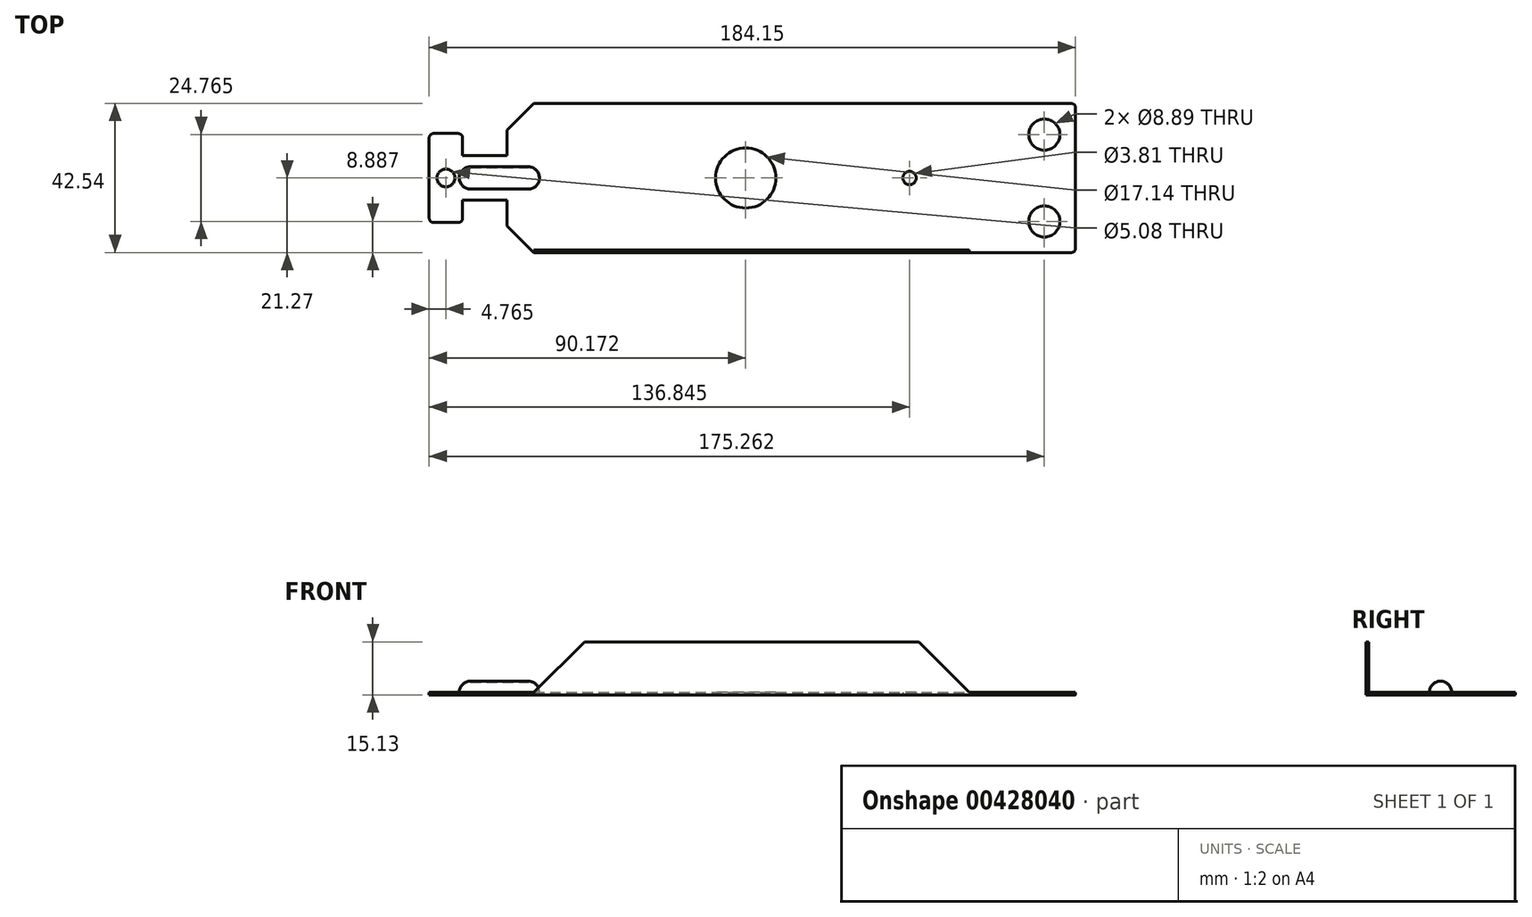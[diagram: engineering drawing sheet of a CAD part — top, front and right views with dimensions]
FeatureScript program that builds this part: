
annotation { "Feature Type Name" : "Feature", "Feature Type Description" : "" }
export const myFeature = defineFeature(function(context is Context, id is Id, definition is map)
    precondition{}
    {
        {
            var Q0;
            Q0=qCreatedBy(makeId("Top.planeOp"),FACE);
            var sketch = newSketch(context, id + "F0", { "sketchPlane" : qUnion([Q0])});
            skLineSegment(sketch, "E0.bottom", {"start": v(-80.96, 21.27) * mm, "end": v(79.7, 21.27) * mm});
            skLineSegment(sketch, "E0.top", {"start": v(-80.96, -21.27) * mm, "end": v(79.7, -21.27) * mm});
            skLineSegment(sketch, "E0.left", {"start": v(-80.96, 21.27) * mm, "end": v(-80.96, -21.27) * mm});
            skLineSegment(sketch, "E0.right", {"start": v(80.96, 20) * mm, "end": v(80.96, -20) * mm});
            skPoint(sketch, "E0.middle", {"position": v(0, 0) * mm});
            skLineSegment(sketch, "E1", {"start": v(-73.34, 21.27) * mm, "end": v(-80.96, 13.65) * mm});
            skLineSegment(sketch, "E2", {"start": v(-80.96, -13.65) * mm, "end": v(-73.34, -21.27) * mm});
            skCircle(sketch, "E3", {"center": v(-13.02, 0) * mm, "radius": 8.57 * mm});
            skCircle(sketch, "E4", {"center": v(33.66, 0) * mm, "radius": 1.9 * mm});
            skCircle(sketch, "E5", {"center": v(72.07, 12.38) * mm, "radius": 4.45 * mm});
            skCircle(sketch, "E6", {"center": v(72.07, -12.38) * mm, "radius": 4.45 * mm});
            skLineSegment(sketch, "E7.bottom", {"start": v(-98.43, 6.35) * mm, "end": v(-63.5, 6.35) * mm});
            skLineSegment(sketch, "E7.top", {"start": v(-98.43, -6.35) * mm, "end": v(-63.5, -6.35) * mm});
            skLineSegment(sketch, "E7.left", {"start": v(-98.43, 6.35) * mm, "end": v(-98.43, -6.35) * mm});
            skLineSegment(sketch, "E7.right", {"start": v(-63.5, 6.35) * mm, "end": v(-63.5, -6.35) * mm});
            skPoint(sketch, "E7.middle", {"position": v(-80.96, 0) * mm});
            skLineSegment(sketch, "E8.bottom", {"start": v(-101.92, 12.7) * mm, "end": v(-94.93, 12.7) * mm});
            skLineSegment(sketch, "E8.top", {"start": v(-101.92, -12.7) * mm, "end": v(-94.93, -12.7) * mm});
            skLineSegment(sketch, "E8.left", {"start": v(-103.19, 11.43) * mm, "end": v(-103.19, -11.43) * mm});
            skLineSegment(sketch, "E8.right", {"start": v(-93.66, 11.43) * mm, "end": v(-93.66, -11.43) * mm});
            skPoint(sketch, "E8.middle", {"position": v(-98.43, 0) * mm});
            skPoint(sketch, "E9.visualSharp", {"position": v(-103.19, 12.7) * mm});
            skArc(sketch, "E9.filletArc", {"start": v(-101.92, 12.7) * mm, "mid": v(-102.82, 12.33) * mm, "end": v(-103.19, 11.43) * mm});
            skPoint(sketch, "E10.visualSharp", {"position": v(-103.19, -12.7) * mm});
            skArc(sketch, "E10.filletArc", {"start": v(-103.19, -11.43) * mm, "mid": v(-102.82, -12.33) * mm, "end": v(-101.92, -12.7) * mm});
            skPoint(sketch, "E11.visualSharp", {"position": v(-93.66, -12.7) * mm});
            skArc(sketch, "E11.filletArc", {"start": v(-94.93, -12.7) * mm, "mid": v(-94.03, -12.33) * mm, "end": v(-93.66, -11.43) * mm});
            skPoint(sketch, "E12.visualSharp", {"position": v(-93.66, 12.7) * mm});
            skArc(sketch, "E12.filletArc", {"start": v(-93.66, 11.43) * mm, "mid": v(-94.03, 12.33) * mm, "end": v(-94.93, 12.7) * mm});
            skPoint(sketch, "E13.visualSharp", {"position": v(80.96, 21.27) * mm});
            skArc(sketch, "E13.filletArc", {"start": v(80.96, 20) * mm, "mid": v(80.6, 20.9) * mm, "end": v(79.7, 21.27) * mm});
            skPoint(sketch, "E14.visualSharp", {"position": v(80.96, -21.27) * mm});
            skArc(sketch, "E14.filletArc", {"start": v(79.7, -21.27) * mm, "mid": v(80.6, -20.9) * mm, "end": v(80.96, -20) * mm});
            skCircle(sketch, "E15", {"center": v(-98.43, 0) * mm, "radius": 2.54 * mm});
            skSolve(sketch);
        }
        {
            var Q0;
            Q0=makeQuery(id+"F0.imprint","IMPRINT",FACE,{"disambiguationData":[TD([[makeQuery(id+"F0.imprint","IMPRINT",EDGE,{"derivedFrom":sQuery(id+"F0.wireOp",EDGE,"E0.right")}),-1.0]])]});
            var Q1;
            {var subQ5=sQuery(id+"F0.wireOp",EDGE,"E7.right");Q1=makeQuery(id+"F0.imprint","IMPRINT",FACE,{"disambiguationData":[TD([[makeQuery(id+"F0.imprint","IMPRINT",EDGE,{"derivedFrom":subQ5}),-1.0]])]});}
            var Q2;
            {var subQ0=sQuery(id+"F0.wireOp",EDGE,"E7.bottom");var subQ1=sQuery(id+"F0.wireOp",EDGE,"E0.left");var subQ2=makeQuery(id+"F0.imprint","INTERSECT",VERTEX,{"derivedFrom":[subQ1,subQ0]});Q2=makeQuery(id+"F0.imprint","IMPRINT",FACE,{"disambiguationData":[TD([[makeQuery(id+"F0.imprint","IMPRINT",EDGE,{"disambiguationData":[TD([[subQ2,-1.0]])],"derivedFrom":subQ1}),-1.0]])]});}
            var Q3;
            {var subQ0=sQuery(id+"F0.wireOp",EDGE,"E7.left");var subQ1=sQuery(id+"F0.wireOp",EDGE,"E7.bottom");var subQ2=makeQuery(id+"F0.imprint","INTERSECT",VERTEX,{"derivedFrom":[subQ1,subQ0]});Q3=makeQuery(id+"F0.imprint","IMPRINT",FACE,{"disambiguationData":[TD([[makeQuery(id+"F0.imprint","IMPRINT",EDGE,{"disambiguationData":[TD([[subQ2,-1.0]])],"derivedFrom":subQ1}),-1.0]])]});}
            var Q4;
            Q4=makeQuery(id+"F0.imprint","IMPRINT",FACE,{"disambiguationData":[TD([[makeQuery(id+"F0.imprint","IMPRINT",EDGE,{"derivedFrom":sQuery(id+"F0.wireOp",EDGE,"E8.bottom")}),-1.0]])]});
            extrude(context, id + "F1", {"entities" : qUnion([Q0, Q1, Q2, Q3, Q4]), "depth" : 0.76 * mm});
        }
        {
            var Q0;
            Q0=makeQuery(id+"F1.opExtrude","SWEPT_FACE",FACE,{"disambiguationData":[OSD([sQuery(id+"F0.wireOp",EDGE,"E0.top")])]});
            var sketch = newSketch(context, id + "F2", { "sketchPlane" : qUnion([Q0])});
            skLineSegment(sketch, "E16", {"start": v(-73.34, 0.76) * mm, "end": v(-58.97, 15.13) * mm});
            skLineSegment(sketch, "E17", {"start": v(-58.97, 15.13) * mm, "end": v(36.28, 15.13) * mm});
            skLineSegment(sketch, "E18", {"start": v(36.28, 15.13) * mm, "end": v(50.64, 0.76) * mm});
            skSolve(sketch);
        }
        {
            var Q0;
            {var subQ0=sQuery(id+"F2.wireOp",EDGE,"E16");Q0=makeQuery(id+"F2.imprint","IMPRINT",FACE,{"disambiguationData":[TD([[makeQuery(id+"F2.imprint","IMPRINT",EDGE,{"derivedFrom":subQ0}),-1.0]])]});}
            extrude(context, id + "F3", {"entities" : qUnion([Q0]), "operationType" : NewBodyOperationType.ADD, "oppositeDirection" : true, "depth" : 0.76 * mm});
        }
        {
            var Q0;
            Q0=makeQuery(id+"F1.opExtrude","CAP_FACE",FACE,{"disambiguationData":[OSD([sQuery(id+"F0.wireOp",EDGE,"E0.bottom"),sQuery(id+"F0.wireOp",EDGE,"E0.top"),sQuery(id+"F0.wireOp",EDGE,"E0.left"),sQuery(id+"F0.wireOp",EDGE,"E0.right"),sQuery(id+"F0.wireOp",EDGE,"E1"),sQuery(id+"F0.wireOp",EDGE,"E2"),sQuery(id+"F0.wireOp",EDGE,"E3"),sQuery(id+"F0.wireOp",EDGE,"E4"),sQuery(id+"F0.wireOp",EDGE,"E5"),sQuery(id+"F0.wireOp",EDGE,"E6"),sQuery(id+"F0.wireOp",EDGE,"E7.bottom"),sQuery(id+"F0.wireOp",EDGE,"E7.top"),sQuery(id+"F0.wireOp",EDGE,"E8.bottom"),sQuery(id+"F0.wireOp",EDGE,"E8.top"),sQuery(id+"F0.wireOp",EDGE,"E8.left"),sQuery(id+"F0.wireOp",EDGE,"E8.right"),sQuery(id+"F0.wireOp",EDGE,"E9.filletArc"),sQuery(id+"F0.wireOp",EDGE,"E10.filletArc"),sQuery(id+"F0.wireOp",EDGE,"E11.filletArc"),sQuery(id+"F0.wireOp",EDGE,"E12.filletArc"),sQuery(id+"F0.wireOp",EDGE,"E13.filletArc"),sQuery(id+"F0.wireOp",EDGE,"E14.filletArc"),sQuery(id+"F0.wireOp",EDGE,"E15")])],"isStart":false});
            var sketch = newSketch(context, id + "F4", { "sketchPlane" : qUnion([Q0])});
            skLineSegment(sketch, "E19.bottom", {"start": v(-91.44, 3.18) * mm, "end": v(-74.93, 3.18) * mm});
            skLineSegment(sketch, "E19.top", {"start": v(-91.44, -3.17) * mm, "end": v(-74.93, -3.17) * mm});
            skLineSegment(sketch, "E19.left", {"start": v(-91.44, 3.18) * mm, "end": v(-91.44, -3.17) * mm});
            skLineSegment(sketch, "E19.right", {"start": v(-74.93, 3.18) * mm, "end": v(-74.93, -3.17) * mm});
            skArc(sketch, "E20", {"start": v(-91.44, 3.18) * mm, "mid": v(-94.62, 0) * mm, "end": v(-91.44, -3.17) * mm});
            skArc(sketch, "E21", {"start": v(-74.93, -3.17) * mm, "mid": v(-71.76, 0) * mm, "end": v(-74.93, 3.18) * mm});
            skArc(sketch, "E22.0.startCap", {"start": v(-91.44, 2.92) * mm, "mid": v(-91.7, 3.18) * mm, "end": v(-91.44, 3.43) * mm});
            skArc(sketch, "E22.0.endCap", {"start": v(-74.93, 3.43) * mm, "mid": v(-74.68, 3.18) * mm, "end": v(-74.93, 2.92) * mm});
            skLineSegment(sketch, "E22.0.left", {"start": v(-91.44, 3.43) * mm, "end": v(-74.93, 3.43) * mm});
            skLineSegment(sketch, "E22.0.right", {"start": v(-91.44, 2.92) * mm, "end": v(-74.93, 2.92) * mm});
            skArc(sketch, "E22.1.startCap", {"start": v(-91.44, 3.43) * mm, "mid": v(-91.19, 3.18) * mm, "end": v(-91.44, 2.92) * mm});
            skArc(sketch, "E22.1.endCap", {"start": v(-91.44, -2.92) * mm, "mid": v(-91.19, -3.17) * mm, "end": v(-91.44, -3.43) * mm});
            skArc(sketch, "E22.1.left", {"start": v(-91.44, 2.92) * mm, "mid": v(-94.36, 0) * mm, "end": v(-91.44, -2.92) * mm});
            skArc(sketch, "E22.1.right", {"start": v(-91.44, 3.43) * mm, "mid": v(-94.87, 0) * mm, "end": v(-91.44, -3.43) * mm});
            skArc(sketch, "E22.2.startCap", {"start": v(-91.44, -3.43) * mm, "mid": v(-91.7, -3.17) * mm, "end": v(-91.44, -2.92) * mm});
            skArc(sketch, "E22.2.endCap", {"start": v(-74.93, -2.92) * mm, "mid": v(-74.68, -3.17) * mm, "end": v(-74.93, -3.43) * mm});
            skLineSegment(sketch, "E22.2.left", {"start": v(-91.44, -2.92) * mm, "end": v(-74.93, -2.92) * mm});
            skLineSegment(sketch, "E22.2.right", {"start": v(-91.44, -3.43) * mm, "end": v(-74.93, -3.43) * mm});
            skArc(sketch, "E22.3.startCap", {"start": v(-74.93, -3.43) * mm, "mid": v(-75.18, -3.17) * mm, "end": v(-74.93, -2.92) * mm});
            skArc(sketch, "E22.3.endCap", {"start": v(-74.93, 2.92) * mm, "mid": v(-75.18, 3.18) * mm, "end": v(-74.93, 3.43) * mm});
            skArc(sketch, "E22.3.left", {"start": v(-74.93, -2.92) * mm, "mid": v(-72, 0) * mm, "end": v(-74.93, 2.92) * mm});
            skArc(sketch, "E22.3.right", {"start": v(-74.93, -3.43) * mm, "mid": v(-71.5, 0) * mm, "end": v(-74.93, 3.43) * mm});
            skLineSegment(sketch, "E23", {"start": v(-91.44, 0) * mm, "end": v(-74.93, 0) * mm});
            skLineSegment(sketch, "E24", {"start": v(-91.44, 0) * mm, "end": v(-94.87, 0) * mm});
            skLineSegment(sketch, "E25", {"start": v(-74.93, 0) * mm, "end": v(-71.5, 0) * mm});
            skSolve(sketch);
        }
        {
            var Q0;
            {var subQ0=sQuery(id+"F4.wireOp",EDGE,"E22.1.left");Q0=makeQuery(id+"F4.imprint","IMPRINT",FACE,{"disambiguationData":[TD([[makeQuery(id+"F4.imprint","IMPRINT",EDGE,{"derivedFrom":subQ0}),1.0]])]});}
            var Q1;
            {var subQ1=sQuery(id+"F4.wireOp",EDGE,"E22.0.right");Q1=makeQuery(id+"F4.imprint","IMPRINT",FACE,{"disambiguationData":[TD([[makeQuery(id+"F4.imprint","IMPRINT",EDGE,{"derivedFrom":subQ1}),-1.0]])]});}
            var Q2;
            {var subQ0=sQuery(id+"F4.wireOp",EDGE,"E22.3.left");Q2=makeQuery(id+"F4.imprint","IMPRINT",FACE,{"disambiguationData":[TD([[makeQuery(id+"F4.imprint","IMPRINT",EDGE,{"derivedFrom":subQ0}),1.0]])]});}
            var Q3;
            {var subQ0=sQuery(id+"F4.wireOp",EDGE,"E22.2.left");Q3=makeQuery(id+"F4.imprint","IMPRINT",FACE,{"disambiguationData":[TD([[makeQuery(id+"F4.imprint","IMPRINT",EDGE,{"derivedFrom":subQ0}),1.0]])]});}
            extrude(context, id + "F5", {"entities" : qUnion([Q0, Q1, Q2, Q3]), "operationType" : NewBodyOperationType.REMOVE, "oppositeDirection" : true, "depth" : 25.4 * mm});
        }
        {
            var Q0;
            {var subQ0=sQuery(id+"F4.wireOp",EDGE,"E22.2.endCap");var subQ1=sQuery(id+"F4.wireOp",EDGE,"E21");var subQ2=makeQuery(id+"F4.imprint","INTERSECT",VERTEX,{"derivedFrom":[subQ1,subQ0]});Q0=makeQuery(id+"F4.imprint","IMPRINT",FACE,{"disambiguationData":[TD([[makeQuery(id+"F4.imprint","IMPRINT",EDGE,{"disambiguationData":[TD([[subQ2,-1.0]])],"derivedFrom":subQ1}),1.0]])]});}
            var Q1;
            {var subQ0=sQuery(id+"F4.wireOp",EDGE,"E21");var subQ3=sQuery(id+"F4.wireOp",EDGE,"E22.2.endCap");var subQ5=makeQuery(id+"F4.imprint","INTERSECT",VERTEX,{"derivedFrom":[subQ0,subQ3]});Q1=makeQuery(id+"F4.imprint","IMPRINT",FACE,{"disambiguationData":[TD([[makeQuery(id+"F4.imprint","IMPRINT",EDGE,{"disambiguationData":[TD([[subQ5,1.0]])],"derivedFrom":subQ0}),1.0]])]});}
            var Q2;
            {var subQ1=sQuery(id+"F4.wireOp",EDGE,"E19.top");var subQ3=sQuery(id+"F4.wireOp",EDGE,"E22.3.startCap");var subQ4=makeQuery(id+"F4.imprint","INTERSECT",VERTEX,{"derivedFrom":[subQ1,subQ3]});Q2=makeQuery(id+"F4.imprint","IMPRINT",FACE,{"disambiguationData":[TD([[makeQuery(id+"F4.imprint","IMPRINT",EDGE,{"disambiguationData":[TD([[subQ4,-1.0]])],"derivedFrom":subQ1}),1.0]])]});}
            var Q3;
            {var subQ5=sQuery(id+"F4.wireOp",EDGE,"E22.2.left");Q3=makeQuery(id+"F4.imprint","IMPRINT",FACE,{"disambiguationData":[TD([[makeQuery(id+"F4.imprint","IMPRINT",EDGE,{"derivedFrom":subQ5}),-1.0]])]});}
            var Q4;
            {var subQ1=sQuery(id+"F4.wireOp",EDGE,"E19.top");var subQ3=sQuery(id+"F4.wireOp",EDGE,"E22.1.endCap");var subQ4=makeQuery(id+"F4.imprint","INTERSECT",VERTEX,{"derivedFrom":[subQ1,subQ3]});Q4=makeQuery(id+"F4.imprint","IMPRINT",FACE,{"disambiguationData":[TD([[makeQuery(id+"F4.imprint","IMPRINT",EDGE,{"disambiguationData":[TD([[subQ4,1.0]])],"derivedFrom":subQ1}),1.0]])]});}
            var Q5;
            {var subQ0=sQuery(id+"F4.wireOp",EDGE,"E20");var subQ3=sQuery(id+"F4.wireOp",EDGE,"E22.2.startCap");var subQ5=makeQuery(id+"F4.imprint","INTERSECT",VERTEX,{"derivedFrom":[subQ0,subQ3]});Q5=makeQuery(id+"F4.imprint","IMPRINT",FACE,{"disambiguationData":[TD([[makeQuery(id+"F4.imprint","IMPRINT",EDGE,{"disambiguationData":[TD([[subQ5,-1.0]])],"derivedFrom":subQ0}),1.0]])]});}
            var Q6;
            {var subQ0=sQuery(id+"F4.wireOp",EDGE,"E24");var subQ1=sQuery(id+"F4.wireOp",EDGE,"E20");var subQ2=makeQuery(id+"F4.imprint","INTERSECT",VERTEX,{"derivedFrom":[subQ1,subQ0]});Q6=makeQuery(id+"F4.imprint","IMPRINT",FACE,{"disambiguationData":[TD([[makeQuery(id+"F4.imprint","IMPRINT",EDGE,{"disambiguationData":[TD([[subQ2,-1.0]])],"derivedFrom":subQ1}),1.0]])]});}
            var Q7;
            Q7=sQuery(id+"F4.wireOp",EDGE,"E23");
            revolve(context, id + "F6", {"operationType" : NewBodyOperationType.ADD, "entities" : qUnion([Q0, Q1, Q2, Q3, Q4, Q5, Q6]), "axis" : qUnion([Q7]), "revolveType" : RevolveType.ONE_DIRECTION, "oppositeDirection" : true, "angle" : 180 * degree});
        }
    });
